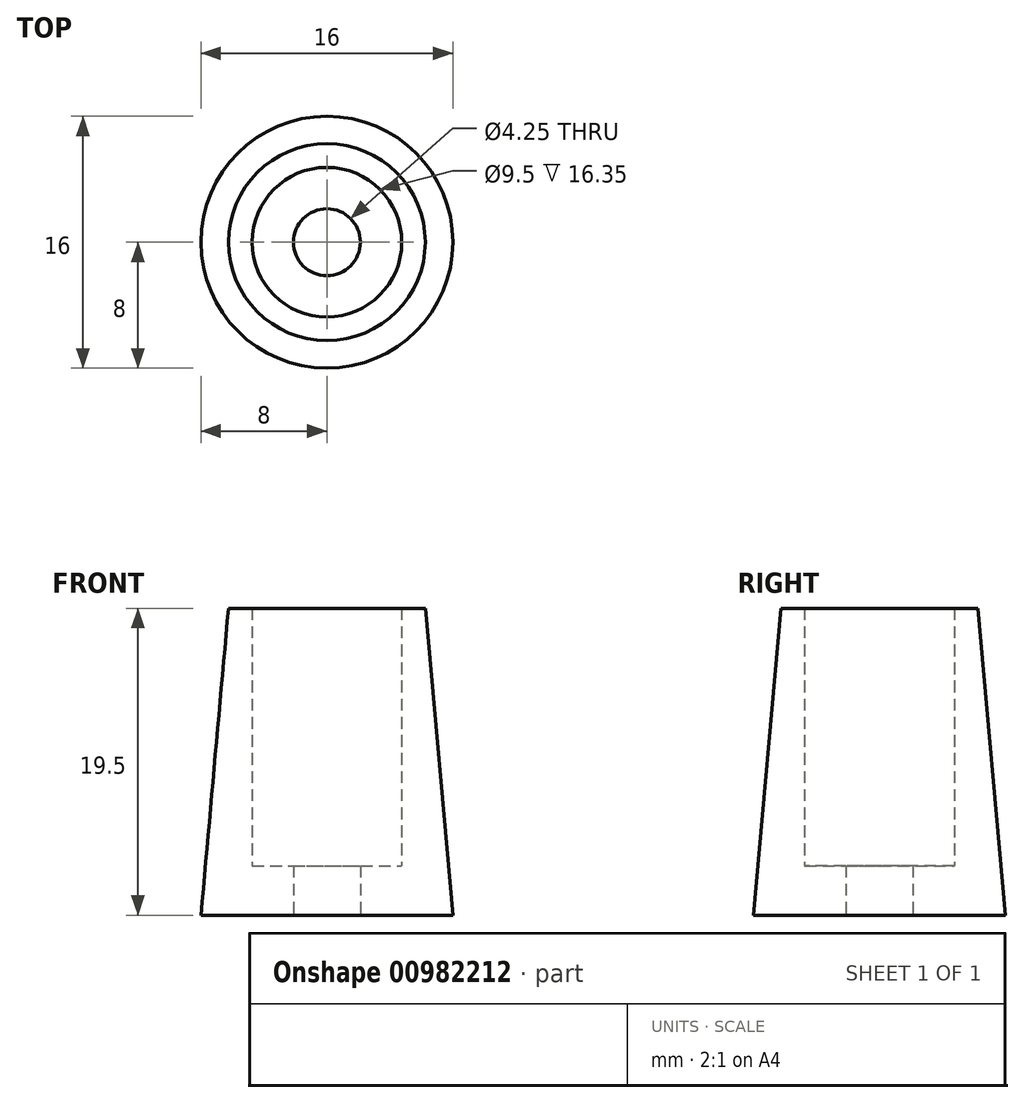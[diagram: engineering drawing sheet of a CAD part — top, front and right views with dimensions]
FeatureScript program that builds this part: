
annotation { "Feature Type Name" : "Feature", "Feature Type Description" : "" }
export const myFeature = defineFeature(function(context is Context, id is Id, definition is map)
    precondition{}
    {
        {
            var Q0;
            Q0=qCreatedBy(makeId("Front.planeOp"),FACE);
            var sketch = newSketch(context, id + "F0", { "sketchPlane" : qUnion([Q0])});
            skLineSegment(sketch, "E0", {"start": v(2.13, 0) * mm, "end": v(2.13, 3.15) * mm});
            skLineSegment(sketch, "E1", {"start": v(2.13, 0) * mm, "end": v(8, 0) * mm});
            skLineSegment(sketch, "E2", {"start": v(4.75, 19.5) * mm, "end": v(6.25, 19.5) * mm});
            skLineSegment(sketch, "E3", {"start": v(6.25, 19.5) * mm, "end": v(8, 0) * mm});
            skLineSegment(sketch, "E4", {"start": v(4.75, 3.15) * mm, "end": v(4.75, 19.5) * mm});
            skLineSegment(sketch, "E5", {"start": v(2.13, 3.15) * mm, "end": v(4.75, 3.15) * mm});
            skLineSegment(sketch, "E6", {"start": v(0, 0) * mm, "end": v(0, 27.32) * mm});
            skSolve(sketch);
        }
        {
            var Q0;
            Q0=makeQuery(id+"F0.imprint","IMPRINT",FACE,{"disambiguationData":[TD([[makeQuery(id+"F0.imprint","IMPRINT",EDGE,{"derivedFrom":sQuery(id+"F0.wireOp",EDGE,"E0")}),-1.0]])]});
            var Q1;
            Q1=sQuery(id+"F0.wireOp",EDGE,"E6");
            revolve(context, id + "F1", {"surfaceOperationType" : NewSurfaceOperationType.NEW, "entities" : qUnion([Q0]), "axis" : qUnion([Q1]), "revolveType" : RevolveType.FULL});
        }
    });
